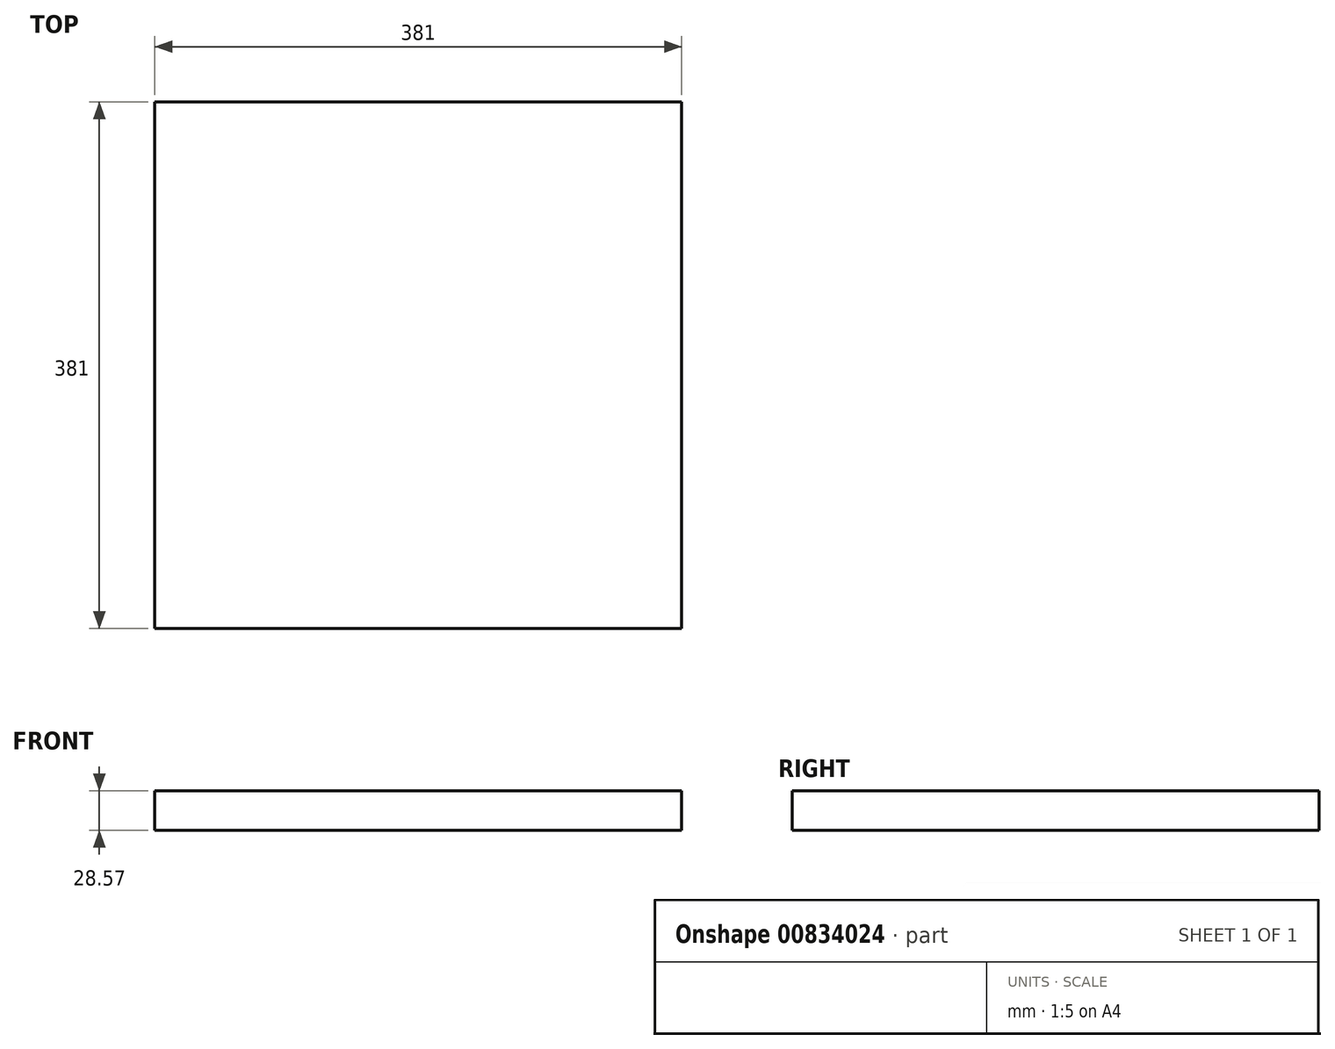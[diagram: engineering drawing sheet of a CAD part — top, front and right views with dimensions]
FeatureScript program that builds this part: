
annotation { "Feature Type Name" : "Feature", "Feature Type Description" : "" }
export const myFeature = defineFeature(function(context is Context, id is Id, definition is map)
    precondition{}
    {
        {
            var Q0;
            Q0=qCreatedBy(makeId("Top.planeOp"),FACE);
            var sketch = newSketch(context, id + "F0", { "sketchPlane" : qUnion([Q0])});
            skLineSegment(sketch, "E0.bottom", {"start": v(190.5, 190.5) * mm, "end": v(-190.5, 190.5) * mm});
            skLineSegment(sketch, "E0.top", {"start": v(190.5, -190.5) * mm, "end": v(-190.5, -190.5) * mm});
            skLineSegment(sketch, "E0.left", {"start": v(190.5, 190.5) * mm, "end": v(190.5, -190.5) * mm});
            skLineSegment(sketch, "E0.right", {"start": v(-190.5, 190.5) * mm, "end": v(-190.5, -190.5) * mm});
            skPoint(sketch, "E0.middle", {"position": v(0, 0) * mm});
            skSolve(sketch);
        }
        {
            var Q0;
            Q0=makeQuery(id+"F0.imprint","IMPRINT",FACE,{"disambiguationData":[TD([[makeQuery(id+"F0.imprint","IMPRINT",EDGE,{"derivedFrom":sQuery(id+"F0.wireOp",EDGE,"E0.bottom")}),1.0]])]});
            extrude(context, id + "F1", {"entities" : qUnion([Q0]), "depth" : 28.57 * mm, "offsetDistance" : 25.4 * mm});
        }
    });
